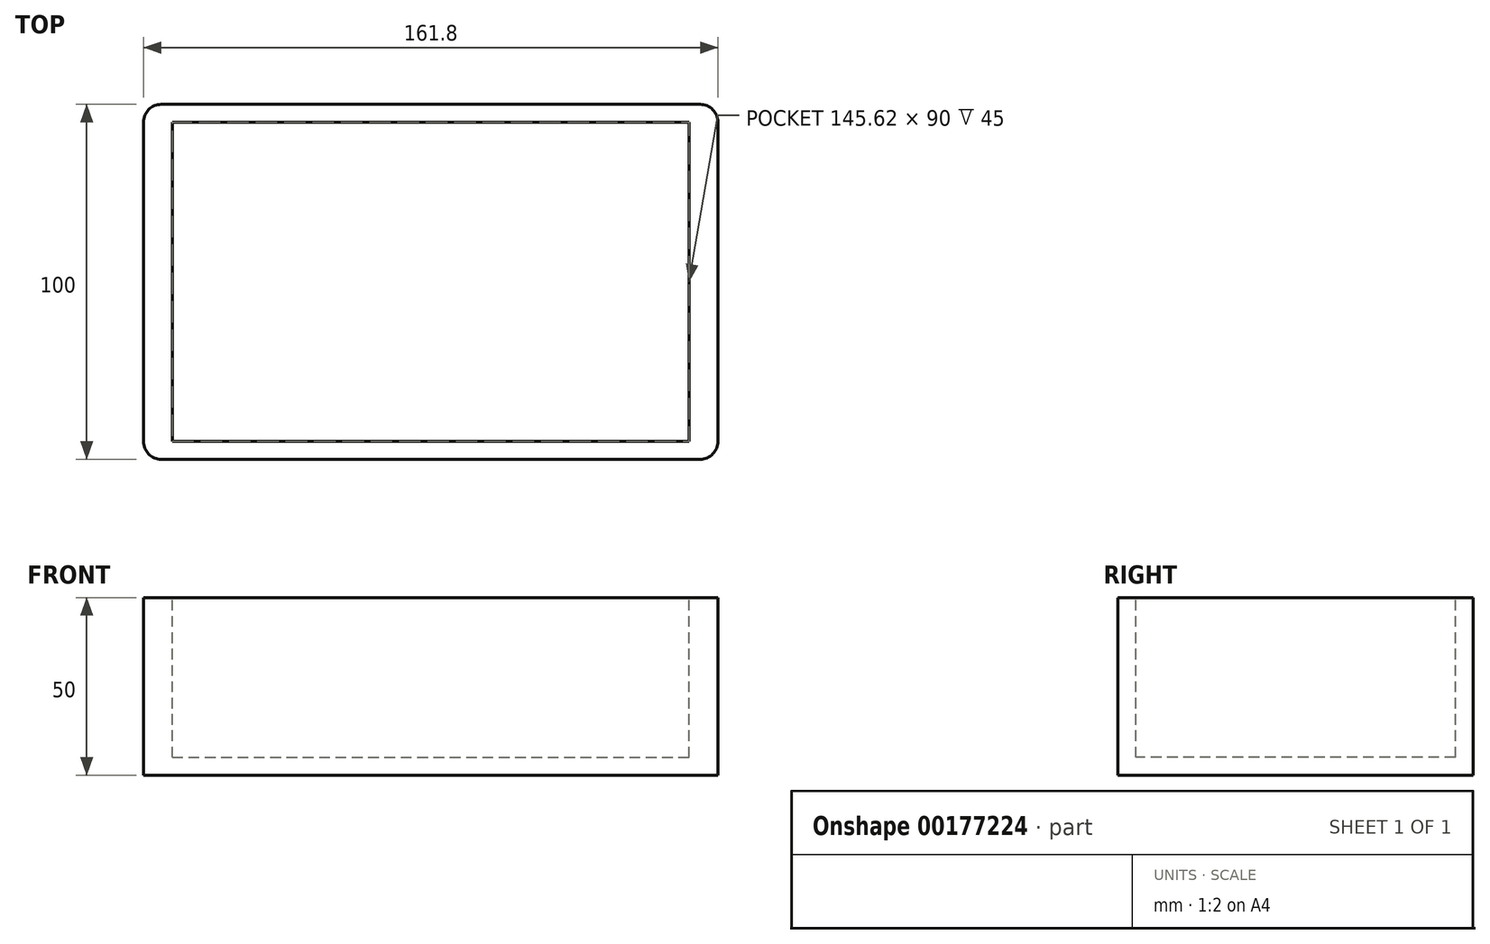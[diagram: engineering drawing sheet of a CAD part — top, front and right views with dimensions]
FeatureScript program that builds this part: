
annotation { "Feature Type Name" : "Feature", "Feature Type Description" : "" }
export const myFeature = defineFeature(function(context is Context, id is Id, definition is map)
    precondition{}
    {
        {
            var Q0;
            Q0=qCreatedBy(makeId("Top.planeOp"),FACE);
            var sketch = newSketch(context, id + "F0", { "sketchPlane" : qUnion([Q0])});
            skLineSegment(sketch, "E0.bottom", {"start": v(-80.9, 50) * mm, "end": v(80.9, 50) * mm});
            skLineSegment(sketch, "E0.top", {"start": v(-80.9, -50) * mm, "end": v(80.9, -50) * mm});
            skLineSegment(sketch, "E0.left", {"start": v(-80.9, 50) * mm, "end": v(-80.9, -50) * mm});
            skLineSegment(sketch, "E0.right", {"start": v(80.9, 50) * mm, "end": v(80.9, -50) * mm});
            skPoint(sketch, "E0.middle", {"position": v(0, 0) * mm});
            skSolve(sketch);
        }
        {
            var Q0;
            Q0 = qSketchRegion(id + "F0", true);
            extrude(context, id + "F1", {"entities" : qUnion([Q0]), "depth" : 50 * mm});
        }
        {
            var Q0;
            Q0=makeQuery(id+"F1.opExtrude","CAP_FACE",FACE,{"disambiguationData":[OSD([sQuery(id+"F0.wireOp",EDGE,"E0.bottom"),sQuery(id+"F0.wireOp",EDGE,"E0.top"),sQuery(id+"F0.wireOp",EDGE,"E0.left"),sQuery(id+"F0.wireOp",EDGE,"E0.right")])],"isStart":false});
            var sketch = newSketch(context, id + "F2", { "sketchPlane" : qUnion([Q0])});
            skLineSegment(sketch, "E1.bottom", {"start": v(-72.8, 45) * mm, "end": v(72.81, 45) * mm});
            skLineSegment(sketch, "E1.top", {"start": v(-72.81, -45) * mm, "end": v(72.8, -45) * mm});
            skLineSegment(sketch, "E1.left", {"start": v(-72.8, 45) * mm, "end": v(-72.81, -45) * mm});
            skLineSegment(sketch, "E1.right", {"start": v(72.81, 45) * mm, "end": v(72.8, -45) * mm});
            skPoint(sketch, "E1.middle", {"position": v(0, 0) * mm});
            skSolve(sketch);
        }
        {
            var Q0;
            Q0 = qSketchRegion(id + "F2", true);
            extrude(context, id + "F3", {"entities" : qUnion([Q0]), "operationType" : NewBodyOperationType.REMOVE, "oppositeDirection" : true, "depth" : 45 * mm});
        }
        {
            var Q0;
            Q0=makeQuery(id+"F1.opExtrude","SWEPT_EDGE",EDGE,{"disambiguationData":[OSD([sQuery(id+"F0.wireOp",EDGE,"E0.top"),sQuery(id+"F0.wireOp",EDGE,"E0.left")])]});
            var Q1;
            Q1=makeQuery(id+"F1.opExtrude","SWEPT_EDGE",EDGE,{"disambiguationData":[OSD([sQuery(id+"F0.wireOp",EDGE,"E0.top"),sQuery(id+"F0.wireOp",EDGE,"E0.right")])]});
            var Q2;
            Q2=makeQuery(id+"F1.opExtrude","SWEPT_EDGE",EDGE,{"disambiguationData":[OSD([sQuery(id+"F0.wireOp",EDGE,"E0.bottom"),sQuery(id+"F0.wireOp",EDGE,"E0.right")])]});
            var Q3;
            Q3=makeQuery(id+"F1.opExtrude","SWEPT_EDGE",EDGE,{"disambiguationData":[OSD([sQuery(id+"F0.wireOp",EDGE,"E0.bottom"),sQuery(id+"F0.wireOp",EDGE,"E0.left")])]});
            fillet(context, id + "F4", {"entities" : qUnion([Q0, Q1, Q2, Q3]), "radius" : 5 * mm, "tangentPropagation" : true, "allowEdgeOverflow" : false});
        }
    });
